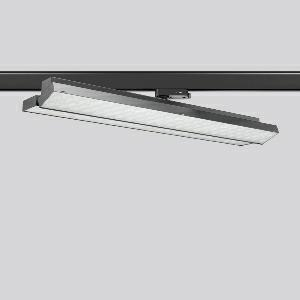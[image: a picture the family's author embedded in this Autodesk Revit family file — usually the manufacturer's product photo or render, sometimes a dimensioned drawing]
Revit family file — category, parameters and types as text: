
# Revit family: tx-move_742163_003_2_c08e
name_source: partatom
category: Lighting Fixtures
units: mm (PartAtom-declared; Revit-internal decimal feet)

## family parameters
Cut with Voids When Loaded = No
Host = Face
Light Source = No
Part Type = Normal
Room Calculation Point = No
Round Connector Dimension = Use Diameter
Shared = No

## types (1)
- MultiLumen 1 (1 x LED Modul 927, 2000 lm, 2700)
    Apparent Load = 38 VA
    CIE Flux Codes = 65 90 98 100 100
    Color Rendering = 92
    Color Temperature = 2700
    Default Elevation = 1800 mm
    Description = Series: TX-MOVE
Multifunctional surface-mounted spotlight for area lighting. Very flat design. Housing: sheet steel, powder-coated. Rotation range: 356°. Swivel range: 90°. Consistent alignment possible with visible tilt scale. High-efficiency LED units with optimum light control thanks to clear plastic (PC) lens optics. Spezielle Mikrostrukturen reduzieren Gelbsaum. Asymmetrical light distribution. Best colour rendering with CRI >90 for fresh products and coloured textiles. With multi adaptor for 3-circuit tracks 230 V. Suitable for Track on ceiling. MultiLumen: Luminous flux adjustable in 3 steps. Factory setting is the highest luminous flux. Environmentally friendly and resource-saving due to replaceable and recyclable components. 
Colour: deep black, matt (RAL 9005)
Length: 570 mm
Width: 119 mm
Height: 92 mm
Lamp: LED
Socket: without socket
Colour temperature: 2700K
Colour rendering index (CRI): 90
System power: 38 W
Rated luminous flux: 4000 lm
Luminous efficiency: 105 lm/W
System power 2: 51 W
Rated luminous flux 2: 5250 lm
Luminous efficiency 2: 103 lm/W
System power 3: 62 W
Rated luminous flux 3: 6200 lm
Luminous efficiency 3: 100 lm/W
Control gear: Regulated power supply
Protection class: I
Type of protection: IP 20
    Height = 75 mm
    Lamp = 1 x LED Modul 927
    Lamp Light Flux = 2000 lm
    Lamp count = 1
    Length = 569 mm
    Lifetime = 50000 h
    Luminous efficacy = 105 lm/W
    Manufacturer = RZB
    ModVariant = No
    Model = 742163.003.2
    Mounting Place = Ceiling
    Mounting Type = Surface mounted
    Number of Poles = 1
    OnlyDefault = Yes
    Power Factor = 1
    Product Name = TX-MOVE
    Product group = Track mounted projectors
    ProductGroupID = 301
    Protection Class = Protection class I
    Protection Degree = IP 20
    RLX_Detail_Level = 1
    RLX_Emergency_Light_Flux = 0 lm
    RLX_Emergency_Type = 0
    RLX_Emergency_Type_DB = No
    RlxData = <blob elided: 57501 chars, md5=5a9ffd50>
    Socket = socket
    Standby Power = 0 W
    System Light Flux = 4000 lm
    System Power = 38 W
    Type Comments = MultiLumen 1
    Type Image = 742162.003.jpg
    URL = http://relux.com
    VarID = multilumen_1
    Voltage = 0 V
    Weight = 0.00 kg
    Width = 119 mm

## geometry (parser evidence)
native form markers: Blend x4, Sweep x15
no freeform markers — native parametric forms only
